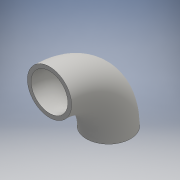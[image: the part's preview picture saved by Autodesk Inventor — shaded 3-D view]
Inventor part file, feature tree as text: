
AUTODESK INVENTOR PART (.ipt)
format: ipt  version: 2016 (Build 200138000, 138)  size: 154,112 bytes
history: native  units: mm
features: sweep x1, sketch x1
ambient origin geometry x8: Origin, YZ Plane, XZ Plane, XY Plane, X Axis, Y Axis, Z Axis, Center Point
bodies: Body1 (feature_tree)
feature tree (2):
  sweep  "Sweep6"
  sketch  "Sketch4"  dims[d23=152.0mm d27=114.0mm d28=9.57mm d29=0.0mm d30=0.0mm]
